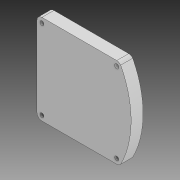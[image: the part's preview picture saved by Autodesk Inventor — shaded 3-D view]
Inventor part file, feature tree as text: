
AUTODESK INVENTOR PART (.ipt)
format: ipt  version: 2021 (Build 250183000, 183)  size: 175,104 bytes
history: native  units: in
note: dims shown in document units (in); Inventor stores cm internally (conversion verified against a paired STEP export)
features: reference x12, extrude x2, sketch x2, fillet x1, projected_geometry x1, other x1
ambient origin geometry x8: Origin, YZ Plane, XZ Plane, XY Plane, X Axis, Y Axis, Z Axis, Center Point
bodies: Solid1 (feature_tree)
feature tree (19):
  extrude  "Extrusion1"  Depth=0.1575in TaperAngle=0.0deg
  extrude  "Extrusion2"  [1 undecoded]
  fillet  "Fillet1"  [1 undecoded]
  sketch  "Sketch1"  dims[d0=0.315in d1=0.0in d2=0.1575in d3=0.0in]
  reference  "Reference1"
  reference  "Reference2"
  reference  "Reference3"
  reference  "Reference4"
  reference  "Reference5"
  reference  "Reference6"
  reference  "Reference7"
  reference  "Reference8"
  reference  "Reference9"
  reference  "Reference10"
  reference  "Reference11"
  reference  "Reference12"
  sketch  "Sketch2"  dims[d4=0.125in]
  projected_geometry  "Projected Loop1"
  other  "Impedance_Analyzer_V2.iam"
note: 2 required parameter values undecoded (feature->parameter linkage not recoverable at this tier; creation-order binding heuristic only, values carry confidence <= 0.55)
